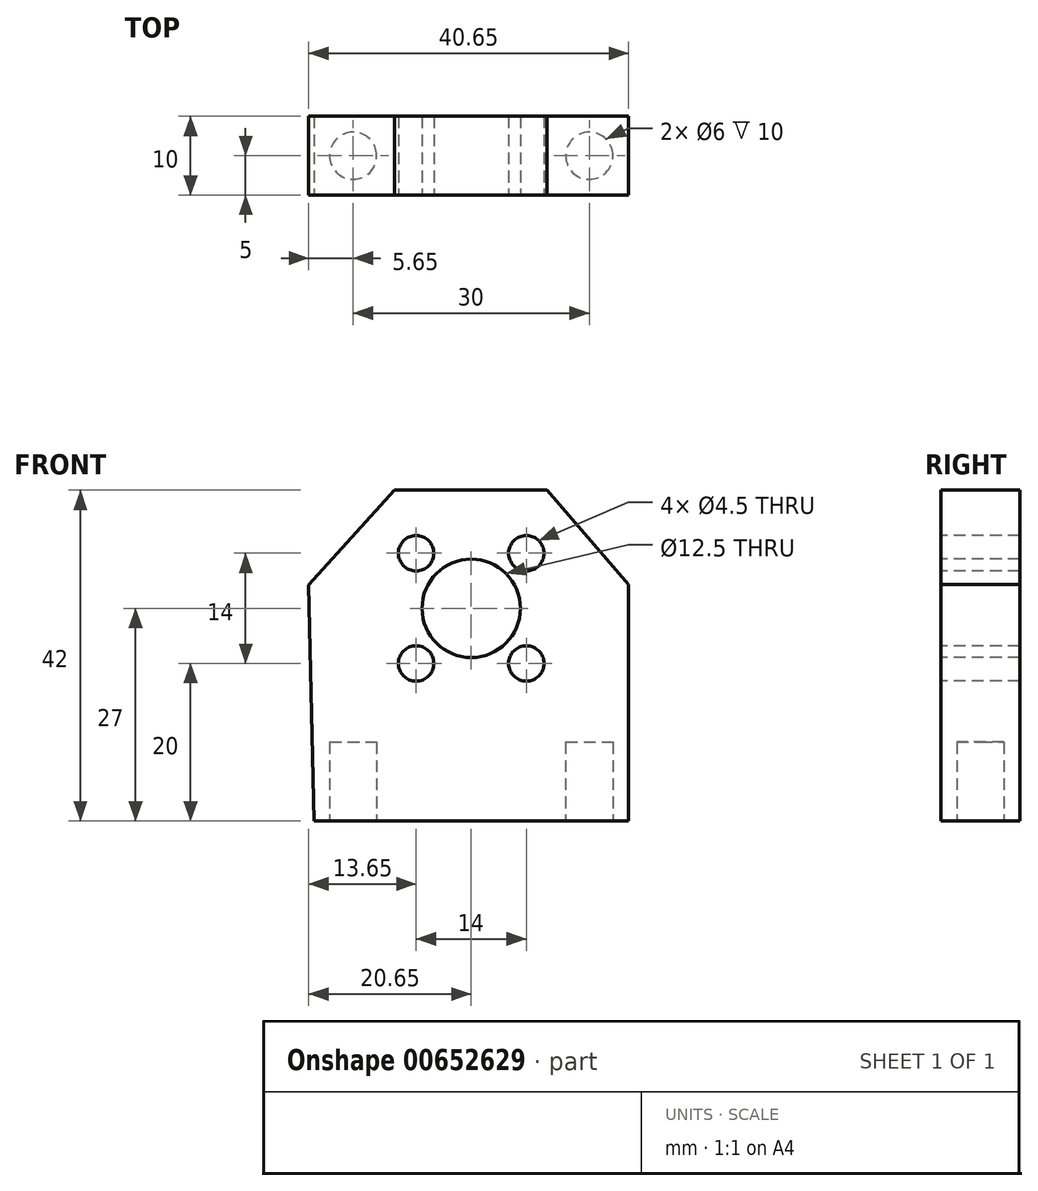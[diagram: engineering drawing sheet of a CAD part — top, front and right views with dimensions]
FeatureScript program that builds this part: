
annotation { "Feature Type Name" : "Feature", "Feature Type Description" : "" }
export const myFeature = defineFeature(function(context is Context, id is Id, definition is map)
    precondition{}
    {
        {
            var Q0;
            Q0=qCreatedBy(makeId("Front.planeOp"),FACE);
            var sketch = newSketch(context, id + "F0", { "sketchPlane" : qUnion([Q0])});
            skLineSegment(sketch, "E0", {"start": v(-20, 0) * mm, "end": v(20, 0) * mm});
            skLineSegment(sketch, "E1", {"start": v(20, 0) * mm, "end": v(20, 30) * mm});
            skLineSegment(sketch, "E2", {"start": v(20, 30) * mm, "end": v(9.61, 42) * mm});
            skLineSegment(sketch, "E3", {"start": v(9.61, 42) * mm, "end": v(-9.72, 42) * mm});
            skLineSegment(sketch, "E4", {"start": v(-9.72, 42) * mm, "end": v(-20.65, 30) * mm});
            skLineSegment(sketch, "E5", {"start": v(-20.65, 30) * mm, "end": v(-20, 0) * mm});
            skCircle(sketch, "E6", {"center": v(0, 27) * mm, "radius": 6.25 * mm});
            skCircle(sketch, "E7", {"center": v(-7, 34) * mm, "radius": 2.25 * mm});
            skCircle(sketch, "E8", {"center": v(7, 34) * mm, "radius": 2.25 * mm});
            skCircle(sketch, "E9", {"center": v(7, 20) * mm, "radius": 2.25 * mm});
            skCircle(sketch, "E10", {"center": v(-7, 20) * mm, "radius": 2.25 * mm});
            skSolve(sketch);
        }
        {
            var Q0;
            Q0 = qSketchRegion(id + "F0", true);
            extrude(context, id + "F1", {"entities" : qUnion([Q0]), "oppositeDirection" : true, "depth" : 10 * mm, "offsetDistance" : 25 * mm});
        }
        {
            var Q0;
            Q0=makeQuery(id+"F1.opExtrude","SWEPT_FACE",FACE,{"disambiguationData":[OSD([sQuery(id+"F0.wireOp",EDGE,"E0")])]});
            var sketch = newSketch(context, id + "F2", { "sketchPlane" : qUnion([Q0])});
            skCircle(sketch, "E11", {"center": v(-15, -5) * mm, "radius": 3 * mm});
            skCircle(sketch, "E12", {"center": v(15, -5) * mm, "radius": 3 * mm});
            skSolve(sketch);
        }
        {
            var Q0;
            Q0=makeQuery(id+"F2.imprint","IMPRINT",FACE,{"disambiguationData":[TD([[makeQuery(id+"F2.imprint","IMPRINT",EDGE,{"derivedFrom":sQuery(id+"F2.wireOp",EDGE,"E11")}),1.0]])]});
            var Q1;
            Q1=makeQuery(id+"F2.imprint","IMPRINT",FACE,{"disambiguationData":[TD([[makeQuery(id+"F2.imprint","IMPRINT",EDGE,{"derivedFrom":sQuery(id+"F2.wireOp",EDGE,"E12")}),1.0]])]});
            extrude(context, id + "F3", {"entities" : qUnion([Q0, Q1]), "operationType" : NewBodyOperationType.REMOVE, "oppositeDirection" : true, "depth" : 10 * mm, "offsetDistance" : 25 * mm});
        }
    });
